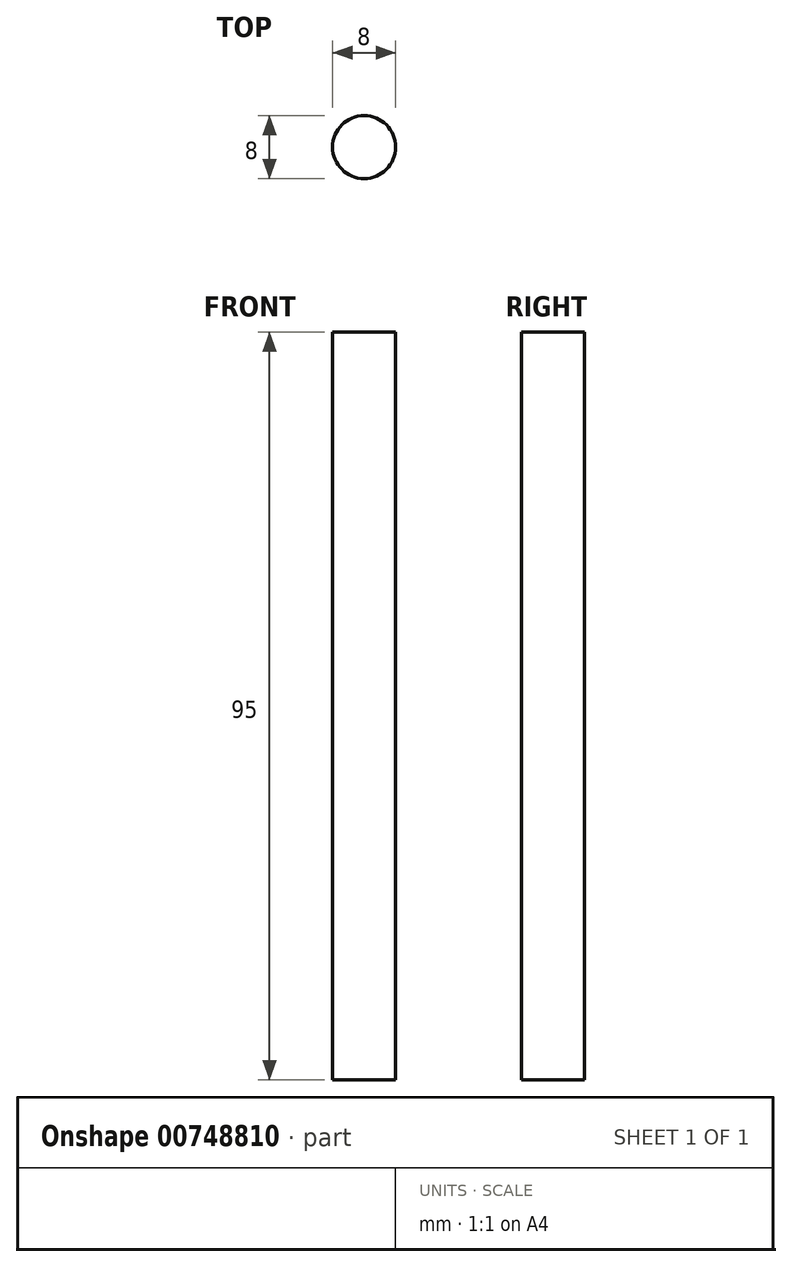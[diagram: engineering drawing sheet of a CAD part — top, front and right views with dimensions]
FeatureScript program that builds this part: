
annotation { "Feature Type Name" : "Feature", "Feature Type Description" : "" }
export const myFeature = defineFeature(function(context is Context, id is Id, definition is map)
    precondition{}
    {
        {
            var Q0;
            Q0=qCreatedBy(makeId("Top.planeOp"),FACE);
            var sketch = newSketch(context, id + "F0", { "sketchPlane" : qUnion([Q0])});
            skCircle(sketch, "E0", {"center": v(0, 0) * mm, "radius": 4 * mm});
            skSolve(sketch);
        }
        {
            var Q0;
            Q0 = qSketchRegion(id + "F0", true);
            extrude(context, id + "F1", {"entities" : qUnion([Q0]), "depth" : 95 * mm, "offsetDistance" : 25 * mm});
        }
    });
